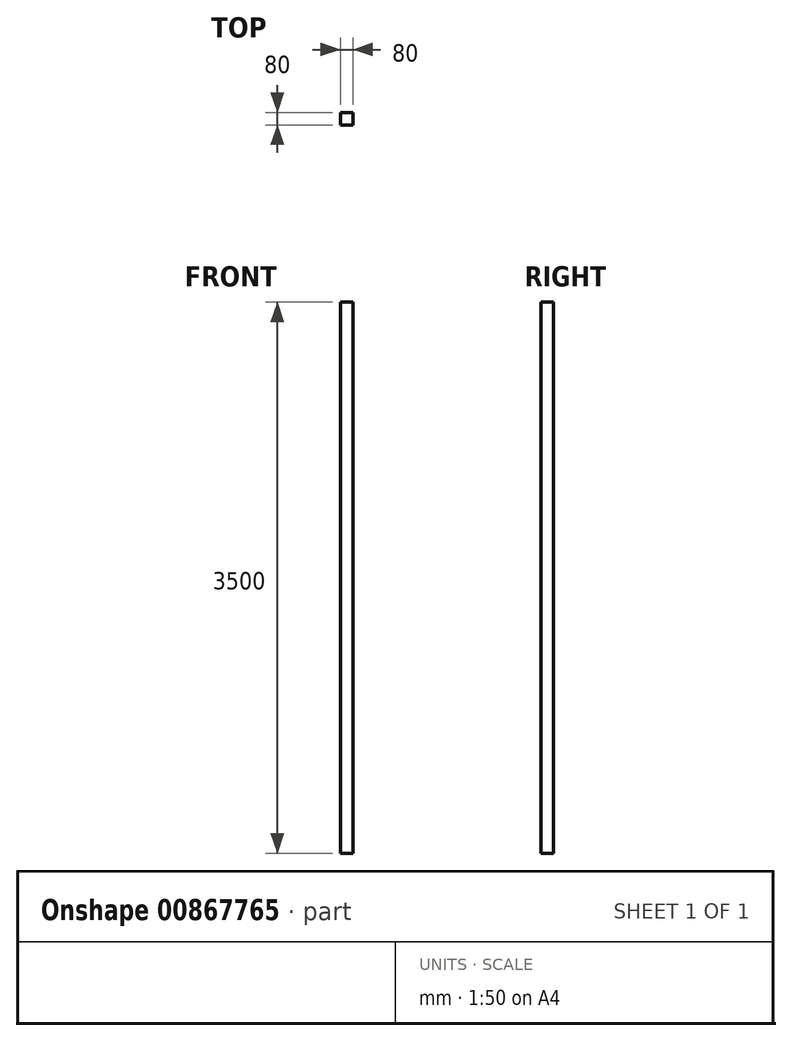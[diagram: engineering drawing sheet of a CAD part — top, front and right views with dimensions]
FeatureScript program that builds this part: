
annotation { "Feature Type Name" : "Feature", "Feature Type Description" : "" }
export const myFeature = defineFeature(function(context is Context, id is Id, definition is map)
    precondition{}
    {
        {
            var Q0;
            Q0=qCreatedBy(makeId("Top.planeOp"),FACE);
            var sketch = newSketch(context, id + "F0", { "sketchPlane" : qUnion([Q0])});
            skLineSegment(sketch, "E0.bottom", {"start": v(40, -40) * mm, "end": v(-40, -40) * mm});
            skLineSegment(sketch, "E0.top", {"start": v(40, 40) * mm, "end": v(-40, 40) * mm});
            skLineSegment(sketch, "E0.left", {"start": v(40, -40) * mm, "end": v(40, 40) * mm});
            skLineSegment(sketch, "E0.right", {"start": v(-40, -40) * mm, "end": v(-40, 40) * mm});
            skPoint(sketch, "E0.middle", {"position": v(0, 0) * mm});
            skSolve(sketch);
        }
        {
            var Q0;
            Q0=makeQuery(id+"F0.imprint","IMPRINT",FACE,{"disambiguationData":[TD([[makeQuery(id+"F0.imprint","IMPRINT",EDGE,{"derivedFrom":sQuery(id+"F0.wireOp",EDGE,"E0.bottom")}),-1.0]])]});
            extrude(context, id + "F1", {"entities" : qUnion([Q0]), "depth" : 3500 * mm, "offsetDistance" : 25 * mm});
        }
    });
